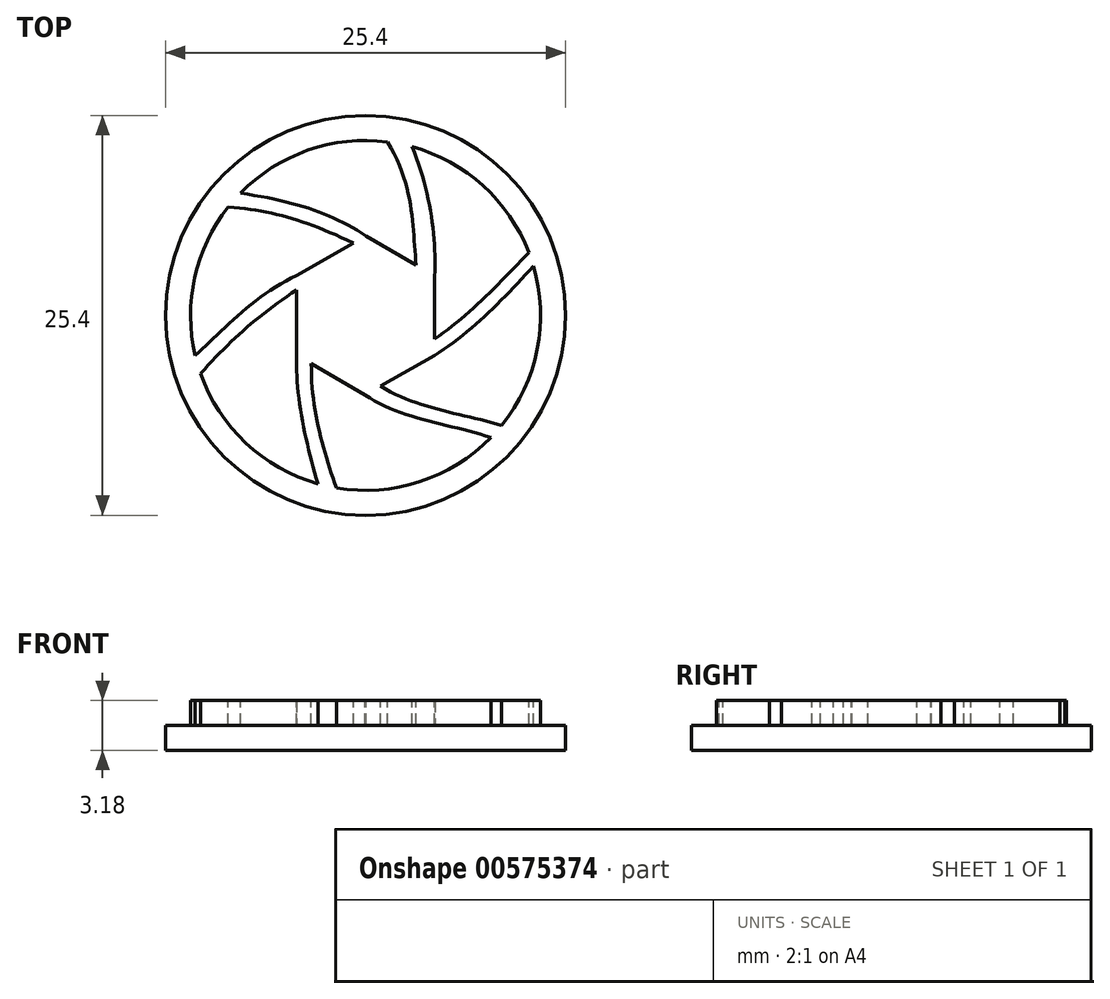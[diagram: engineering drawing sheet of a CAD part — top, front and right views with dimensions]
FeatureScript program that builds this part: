
annotation { "Feature Type Name" : "Feature", "Feature Type Description" : "" }
export const myFeature = defineFeature(function(context is Context, id is Id, definition is map)
    precondition{}
    {
        {
            var Q0;
            Q0=qCreatedBy(makeId("Top.planeOp"),FACE);
            var sketch = newSketch(context, id + "F0", { "sketchPlane" : qUnion([Q0])});
            skCircle(sketch, "E0", {"center": v(0, 0) * mm, "radius": 12.7 * mm});
            skSolve(sketch);
        }
        {
            var Q0;
            Q0 = qSketchRegion(id + "F0", true);
            extrude(context, id + "F1", {"entities" : qUnion([Q0]), "depth" : 3.17 * mm, "offsetDistance" : 25.4 * mm});
        }
        {
            var Q0;
            Q0=makeQuery(id+"F1.opExtrude","CAP_FACE",FACE,{"disambiguationData":[OSD([sQuery(id+"F0.wireOp",EDGE,"E0")])],"isStart":false});
            var sketch = newSketch(context, id + "F2", { "sketchPlane" : qUnion([Q0])});
            skCircle(sketch, "E1", {"center": v(0, 0) * mm, "radius": 12.7 * mm});
            skCircle(sketch, "E2", {"center": v(0, 0) * mm, "radius": 11.11 * mm});
            skCircle(sketch, "E3.cCircle", {"center": v(0, 0) * mm, "radius": 4.38 * mm, "construction": true});
            skLineSegment(sketch, "E3.0", {"start": v(0.02, 5.05) * mm, "end": v(4.39, 2.51) * mm});
            skLineSegment(sketch, "E3.1", {"start": v(4.39, 2.51) * mm, "end": v(4.37, -2.54) * mm});
            skLineSegment(sketch, "E3.2", {"start": v(4.37, -2.54) * mm, "end": v(-0.02, -5.05) * mm});
            skLineSegment(sketch, "E3.3", {"start": v(-0.02, -5.05) * mm, "end": v(-4.39, -2.51) * mm});
            skLineSegment(sketch, "E3.4", {"start": v(-4.39, -2.51) * mm, "end": v(-4.37, 2.54) * mm});
            skLineSegment(sketch, "E3.5", {"start": v(-4.37, 2.54) * mm, "end": v(0.02, 5.05) * mm});
            skPoint(sketch, "E3.0.midPoint", {"position": v(2.2, 3.78) * mm});
            skFitSpline(sketch, "E4", {"points": [v(-8.73, 6.88) * mm, v(-0.77, 4.6) * mm], "startDerivative": vector(8.49, -0.58) * mm, "endDerivative": vector(9.12, -4.28) * mm});
            skFitSpline(sketch, "E5", {"points": [v(-7.95, 7.76) * mm, v(0.02, 5.05) * mm], "startDerivative": vector(10.52, -1.48) * mm, "endDerivative": vector(6.47, -4.2) * mm});
            skFitSpline(sketch, "E6", {"points": [v(1.38, 11.03) * mm, v(3.22, 3.2) * mm], "startDerivative": vector(5.34, -8.84) * mm, "endDerivative": vector(0.79, -6.96) * mm});
            skFitSpline(sketch, "E7", {"points": [v(2.96, 10.71) * mm, v(4.39, 2.51) * mm], "startDerivative": vector(3.47, -8.44) * mm, "endDerivative": vector(-0.37, -7.3) * mm});
            skFitSpline(sketch, "E8", {"points": [v(10.37, 4) * mm, v(4.37, -1.5) * mm], "startDerivative": vector(-5.6, -5.86) * mm, "endDerivative": vector(-6.66, -4.49) * mm});
            skFitSpline(sketch, "E9", {"points": [v(10.66, 3.14) * mm, v(4.37, -2.54) * mm], "startDerivative": vector(-5.8, -6.4) * mm, "endDerivative": vector(-7.16, -4.5) * mm});
            skFitSpline(sketch, "E10", {"points": [v(8.65, -6.98) * mm, v(0.95, -4.5) * mm], "startDerivative": vector(-7.58, 2.3) * mm, "endDerivative": vector(-7.12, 4.4) * mm});
            skFitSpline(sketch, "E11", {"points": [v(7.96, -7.75) * mm, v(-0.02, -5.05) * mm], "startDerivative": vector(-7.64, 2.58) * mm, "endDerivative": vector(-6.56, 4.63) * mm});
            skFitSpline(sketch, "E12", {"points": [v(-1.85, -10.96) * mm, v(-3.45, -3.06) * mm], "startDerivative": vector(-2.56, 7.27) * mm, "endDerivative": vector(0, 8.89) * mm});
            skFitSpline(sketch, "E13", {"points": [v(-3.02, -10.7) * mm, v(-4.39, -2.51) * mm], "startDerivative": vector(-2.46, 8.13) * mm, "endDerivative": vector(0.21, 7.55) * mm});
            skFitSpline(sketch, "E14", {"points": [v(-10.48, -3.69) * mm, v(-4.37, 1.62) * mm], "startDerivative": vector(5.63, 6.21) * mm, "endDerivative": vector(7.4, 4.87) * mm});
            skFitSpline(sketch, "E15", {"points": [v(-10.82, -2.54) * mm, v(-4.37, 2.54) * mm], "startDerivative": vector(5, 4.5) * mm, "endDerivative": vector(8.15, 3.73) * mm});
            skSolve(sketch);
        }
        {
            var Q0;
            {var subQ12=sQuery(id+"F2.wireOp",EDGE,"E3.0");var subQ14=makeQuery(id+"F2.imprint","INTERSECT",VERTEX,{"derivedFrom":[subQ12,sQuery(id+"F2.wireOp",EDGE,"E6")]});Q0=makeQuery(id+"F2.imprint","IMPRINT",FACE,{"disambiguationData":[TD([[makeQuery(id+"F2.imprint","IMPRINT",EDGE,{"disambiguationData":[TD([[subQ14,1.0]])],"derivedFrom":subQ12}),-1.0]])]});}
            var Q1;
            {var subQ0=sQuery(id+"F2.wireOp",EDGE,"E4");Q1=makeQuery(id+"F2.imprint","IMPRINT",FACE,{"disambiguationData":[TD([[makeQuery(id+"F2.imprint","IMPRINT",EDGE,{"derivedFrom":subQ0}),1.0]])]});}
            var Q2;
            {var subQ0=sQuery(id+"F2.wireOp",EDGE,"E6");Q2=makeQuery(id+"F2.imprint","IMPRINT",FACE,{"disambiguationData":[TD([[makeQuery(id+"F2.imprint","IMPRINT",EDGE,{"derivedFrom":subQ0}),1.0]])]});}
            var Q3;
            {var subQ0=sQuery(id+"F2.wireOp",EDGE,"E8");Q3=makeQuery(id+"F2.imprint","IMPRINT",FACE,{"disambiguationData":[TD([[makeQuery(id+"F2.imprint","IMPRINT",EDGE,{"derivedFrom":subQ0}),1.0]])]});}
            var Q4;
            {var subQ0=sQuery(id+"F2.wireOp",EDGE,"E12");Q4=makeQuery(id+"F2.imprint","IMPRINT",FACE,{"disambiguationData":[TD([[makeQuery(id+"F2.imprint","IMPRINT",EDGE,{"derivedFrom":subQ0}),1.0]])]});}
            var Q5;
            {var subQ0=sQuery(id+"F2.wireOp",EDGE,"E14");Q5=makeQuery(id+"F2.imprint","IMPRINT",FACE,{"disambiguationData":[TD([[makeQuery(id+"F2.imprint","IMPRINT",EDGE,{"derivedFrom":subQ0}),1.0]])]});}
            var Q6;
            {var subQ0=sQuery(id+"F2.wireOp",EDGE,"E10");Q6=makeQuery(id+"F2.imprint","IMPRINT",FACE,{"disambiguationData":[TD([[makeQuery(id+"F2.imprint","IMPRINT",EDGE,{"derivedFrom":subQ0}),1.0]])]});}
            var Q7;
            Q7=makeQuery(id+"F2.imprint","IMPRINT",FACE,{"disambiguationData":[TD([[makeQuery(id+"F2.imprint","IMPRINT",EDGE,{"derivedFrom":sQuery(id+"F2.wireOp",EDGE,"E1")}),1.0]])]});
            extrude(context, id + "F3", {"entities" : qUnion([Q0, Q1, Q2, Q3, Q4, Q5, Q6, Q7]), "operationType" : NewBodyOperationType.REMOVE, "oppositeDirection" : true, "depth" : 1.59 * mm, "offsetDistance" : 25.4 * mm});
        }
    });
